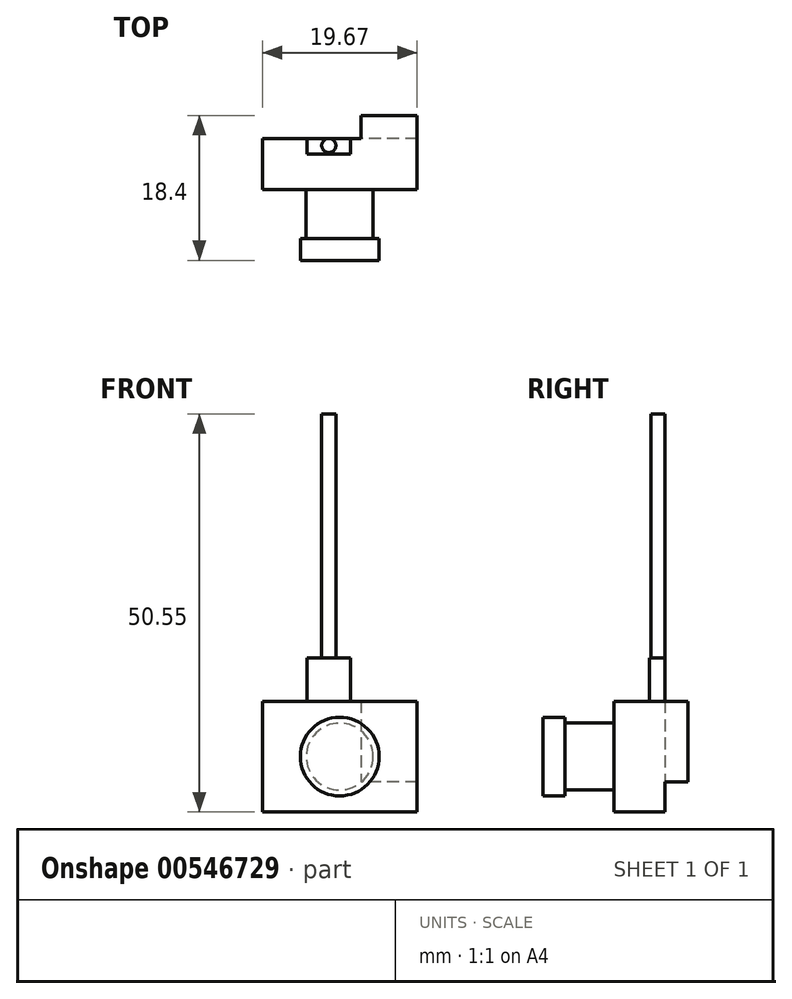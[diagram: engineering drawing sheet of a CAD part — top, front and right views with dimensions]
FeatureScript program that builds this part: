
annotation { "Feature Type Name" : "Feature", "Feature Type Description" : "" }
export const myFeature = defineFeature(function(context is Context, id is Id, definition is map)
    precondition{}
    {
        {
            var Q0;
            Q0=qCreatedBy(makeId("Front.planeOp"),FACE);
            var sketch = newSketch(context, id + "F0", { "sketchPlane" : qUnion([Q0])});
            skLineSegment(sketch, "E0.bottom", {"start": v(0, 0) * mm, "end": v(19.67, 0) * mm});
            skLineSegment(sketch, "E0.top", {"start": v(0, -14.05) * mm, "end": v(19.67, -14.05) * mm});
            skLineSegment(sketch, "E0.left", {"start": v(0, 0) * mm, "end": v(0, -14.05) * mm});
            skLineSegment(sketch, "E0.right", {"start": v(19.67, 0) * mm, "end": v(19.67, -14.05) * mm});
            skLineSegment(sketch, "E1", {"start": v(0, 0) * mm, "end": v(19.67, -14.05) * mm, "construction": true});
            skLineSegment(sketch, "E2", {"start": v(0, -14.05) * mm, "end": v(19.67, 0) * mm, "construction": true});
            skCircle(sketch, "E3", {"center": v(9.84, -7.02) * mm, "radius": 4.25 * mm});
            skSolve(sketch);
        }
        {
            var Q0;
            Q0 = qSketchRegion(id + "F0", true);
            var Q1;
            Q1=makeQuery(id+"F0.imprint","IMPRINT",FACE,{"disambiguationData":[TD([[makeQuery(id+"F0.imprint","IMPRINT",EDGE,{"derivedFrom":sQuery(id+"F0.wireOp",EDGE,"E3")}),1.0]])]});
            extrude(context, id + "F1", {"entities" : qUnion([Q0, Q1]), "depth" : 6.5 * mm, "offsetDistance" : 25 * mm});
        }
        {
            var Q0;
            Q0=makeQuery(id+"F0.imprint","IMPRINT",FACE,{"disambiguationData":[TD([[makeQuery(id+"F0.imprint","IMPRINT",EDGE,{"derivedFrom":sQuery(id+"F0.wireOp",EDGE,"E3")}),1.0]])]});
            extrude(context, id + "F2", {"entities" : qUnion([Q0]), "operationType" : NewBodyOperationType.ADD, "depth" : 15.5 * mm, "offsetDistance" : 25 * mm});
        }
        {
            var Q0;
            Q0=makeQuery(id+"F2.opExtrude","CAP_FACE",FACE,{"disambiguationData":[OSD([sQuery(id+"F0.wireOp",EDGE,"E3")])],"isStart":false});
            var sketch = newSketch(context, id + "F3", { "sketchPlane" : qUnion([Q0])});
            skCircle(sketch, "E4", {"center": v(9.84, -7.02) * mm, "radius": 5 * mm});
            skSolve(sketch);
        }
        {
            var Q0;
            Q0 = qSketchRegion(id + "F3", true);
            extrude(context, id + "F4", {"entities" : qUnion([Q0]), "operationType" : NewBodyOperationType.ADD, "oppositeDirection" : true, "depth" : 2.78 * mm, "offsetDistance" : 25 * mm});
        }
        {
            var Q0;
            Q0=makeQuery(id+"F1.opExtrude","CAP_FACE",FACE,{"disambiguationData":[OSD([sQuery(id+"F0.wireOp",EDGE,"E0.bottom"),sQuery(id+"F0.wireOp",EDGE,"E0.top"),sQuery(id+"F0.wireOp",EDGE,"E0.left"),sQuery(id+"F0.wireOp",EDGE,"E0.right")])],"isStart":true});
            var sketch = newSketch(context, id + "F5", { "sketchPlane" : qUnion([Q0])});
            skLineSegment(sketch, "E5.bottom", {"start": v(-19.67, 0) * mm, "end": v(-12.57, 0) * mm});
            skLineSegment(sketch, "E5.top", {"start": v(-19.67, -10.22) * mm, "end": v(-12.57, -10.22) * mm});
            skLineSegment(sketch, "E5.left", {"start": v(-19.67, 0) * mm, "end": v(-19.67, -10.22) * mm});
            skLineSegment(sketch, "E5.right", {"start": v(-12.57, 0) * mm, "end": v(-12.57, -10.22) * mm});
            skSolve(sketch);
        }
        {
            var Q0;
            Q0=makeQuery(id+"F5.imprint","IMPRINT",FACE,{"disambiguationData":[TD([[makeQuery(id+"F5.imprint","IMPRINT",EDGE,{"derivedFrom":sQuery(id+"F5.wireOp",EDGE,"E5.bottom")}),1.0]])]});
            extrude(context, id + "F6", {"entities" : qUnion([Q0]), "operationType" : NewBodyOperationType.ADD, "depth" : 2.9 * mm, "offsetDistance" : 25 * mm});
        }
        {
            var Q0;
            Q0=makeQuery(id+"F6.boolean.opBoolean","MERGE",FACE,{"derivedFrom":[makeQuery(id+"F1.opExtrude","SWEPT_FACE",FACE,{"disambiguationData":[OSD([sQuery(id+"F0.wireOp",EDGE,"E0.bottom")])]}),makeQuery(id+"F6.opExtrude","SWEPT_FACE",FACE,{"disambiguationData":[OSD([sQuery(id+"F5.wireOp",EDGE,"E5.bottom")])]})]});
            var sketch = newSketch(context, id + "F7", { "sketchPlane" : qUnion([Q0])});
            skLineSegment(sketch, "E6.bottom", {"start": v(5.7, 0) * mm, "end": v(11.2, 0) * mm});
            skLineSegment(sketch, "E6.top", {"start": v(5.7, -2) * mm, "end": v(11.2, -2) * mm});
            skLineSegment(sketch, "E6.left", {"start": v(5.7, 0) * mm, "end": v(5.7, -2) * mm});
            skLineSegment(sketch, "E6.right", {"start": v(11.2, 0) * mm, "end": v(11.2, -2) * mm});
            skSolve(sketch);
        }
        {
            var Q0;
            Q0=makeQuery(id+"F7.imprint","IMPRINT",FACE,{"disambiguationData":[TD([[makeQuery(id+"F7.imprint","IMPRINT",EDGE,{"derivedFrom":sQuery(id+"F7.wireOp",EDGE,"E6.bottom")}),-1.0]])]});
            extrude(context, id + "F8", {"entities" : qUnion([Q0]), "operationType" : NewBodyOperationType.ADD, "depth" : 5.5 * mm, "offsetDistance" : 25 * mm});
        }
        {
            var Q0;
            Q0=makeQuery(id+"F8.opExtrude","CAP_FACE",FACE,{"disambiguationData":[OSD([sQuery(id+"F7.wireOp",EDGE,"E6.bottom"),sQuery(id+"F7.wireOp",EDGE,"E6.top"),sQuery(id+"F7.wireOp",EDGE,"E6.left"),sQuery(id+"F7.wireOp",EDGE,"E6.right")])],"isStart":false});
            var sketch = newSketch(context, id + "F9", { "sketchPlane" : qUnion([Q0])});
            skCircle(sketch, "E7", {"center": v(8.45, -0.9) * mm, "radius": 0.9 * mm});
            skPoint(sketch, "E7.centerSnap0", {"position": v(8.45, 0) * mm});
            skSolve(sketch);
        }
        {
            var Q0;
            Q0=makeQuery(id+"F9.imprint","IMPRINT",FACE,{"disambiguationData":[TD([[makeQuery(id+"F9.imprint","IMPRINT",EDGE,{"derivedFrom":sQuery(id+"F9.wireOp",EDGE,"E7")}),1.0]])]});
            extrude(context, id + "F10", {"entities" : qUnion([Q0]), "operationType" : NewBodyOperationType.ADD, "depth" : 31 * mm, "offsetDistance" : 25 * mm});
        }
    });
